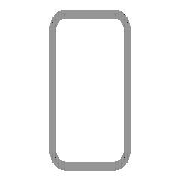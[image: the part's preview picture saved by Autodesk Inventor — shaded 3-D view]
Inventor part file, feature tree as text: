
AUTODESK INVENTOR PART (.ipt)
format: ipt  version: 2025.3 (Build 293356000, 356)  size: 135,680 bytes
history: native  units: mm (DEFAULTED — no unit token found)
features: other x4, sketch x1, plane x1
ambient origin geometry x8: Origin, YZ Plane, XZ Plane, XY Plane, X Axis, Y Axis, Z Axis, Center Point
bodies: Solid1 (feature_tree), Body (feature_tree)
feature tree (6):
  parser-record x1  (decoder bookkeeping rows leaked as tree rows — omitted from the tree; the rows remain in map.json)
  other  "Driven Length"
  other  "Start Plane"
  other  "End Plane"
  sketch  "Sketch3"  dims[d3=470.0mm d4=0.0mm d7=6.0mm d9=40.0mm d11=80.0mm d12=3.0mm d13=20.0mm d14=490.0mm d15=20.0mm d16=40.0mm d17=90.0deg d18=470.0mm]
  plane  "Work Plane3"
